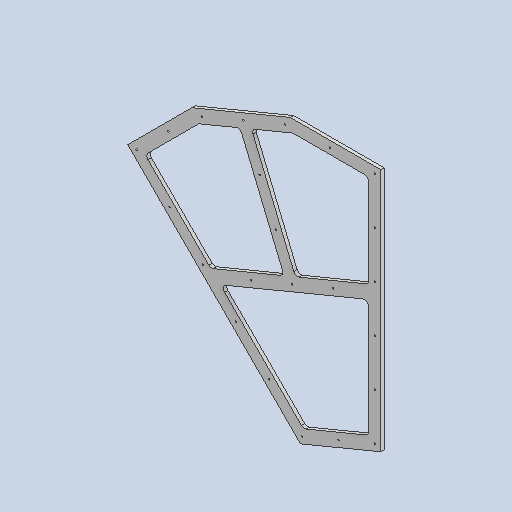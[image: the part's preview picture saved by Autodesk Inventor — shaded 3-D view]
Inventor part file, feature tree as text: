
AUTODESK INVENTOR PART (.ipt)
format: ipt  version: 2025 (Build 290162010, 162A)  size: 171,008 bytes
history: native  units: mm
features: other x3, sketch x2
ambient origin geometry x8: Origin, YZ Plane, XZ Plane, XY Plane, X Axis, Y Axis, Z Axis, Center Point
bodies: Solid1 (feature_tree)
feature tree (5):
  other  "ДМС 206 Крепление сетки к кассете"
  other  "Solid1::ДМС 206 Крепление сетки к кассете"
  other  "TaggingFeature1"
  sketch  "Sketch1"  dims[d0=10.0mm]
  sketch  "Sketch2"
